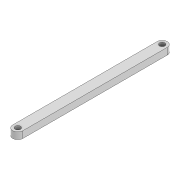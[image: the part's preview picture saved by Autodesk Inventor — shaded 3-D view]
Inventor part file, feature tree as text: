
AUTODESK INVENTOR PART (.ipt)
format: ipt  version: 2022 (Build 260153000, 153)  size: 88,064 bytes
history: native  units: mm
features: extrude x1, sketch x1
ambient origin geometry x8: Origin, YZ Plane, XZ Plane, XY Plane, X Axis, Y Axis, Z Axis, Center Point
bodies: Solid1 (feature_tree)
feature tree (2):
  extrude  "Extrusion1"  Depth=4.0mm
  sketch  "Sketch1"  dims[d0=3.2mm d1=3.2mm d2=6.0mm d3=85.9mm d6=4.0mm d7=0.0mm]
